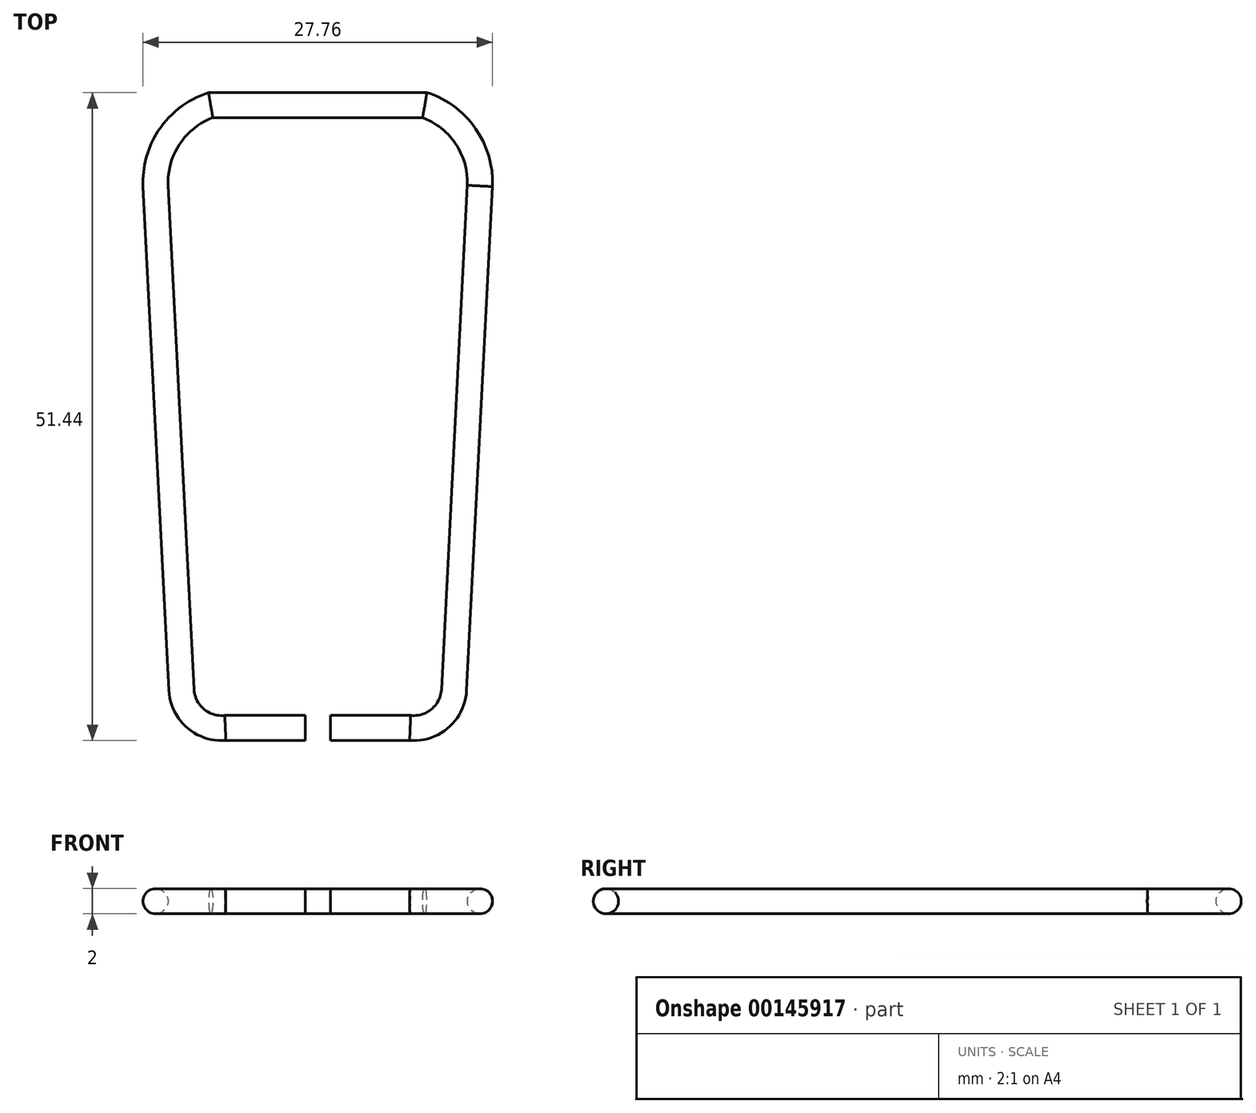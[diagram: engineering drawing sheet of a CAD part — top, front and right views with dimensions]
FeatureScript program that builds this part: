
annotation { "Feature Type Name" : "Feature", "Feature Type Description" : "" }
export const myFeature = defineFeature(function(context is Context, id is Id, definition is map)
    precondition{}
    {
        {
            var Q0;
            Q0=qCreatedBy(makeId("Top.planeOp"),FACE);
            var sketch = newSketch(context, id + "F0", { "sketchPlane" : qUnion([Q0])});
            skArc(sketch, "E0.0", {"start": v(-8.5, 33.52) * mm, "mid": v(-11.75, 31.03) * mm, "end": v(-12.88, 27.1) * mm});
            skLineSegment(sketch, "E0.2", {"start": v(-12.88, 27.1) * mm, "end": v(-10.82, -12.9) * mm});
            skArc(sketch, "E0.4", {"start": v(-10.82, -12.9) * mm, "mid": v(-9.72, -15.15) * mm, "end": v(-7.34, -15.92) * mm});
            skPoint(sketch, "E1.end.orphan", {"position": v(-15, 25.17) * mm});
            skLineSegment(sketch, "E2", {"start": v(-7.34, -15.92) * mm, "end": v(-1, -15.92) * mm});
            skPoint(sketch, "E3", {"position": v(-11.48, 0) * mm});
            skArc(sketch, "E4.MirrorCS", {"start": v(8.5, 33.52) * mm, "mid": v(11.75, 31.03) * mm, "end": v(12.88, 27.1) * mm});
            skLineSegment(sketch, "E5.MirrorCS", {"start": v(12.88, 27.1) * mm, "end": v(10.82, -12.9) * mm});
            skArc(sketch, "E6.MirrorCS", {"start": v(10.82, -12.9) * mm, "mid": v(9.72, -15.15) * mm, "end": v(7.34, -15.92) * mm});
            skLineSegment(sketch, "E7.MirrorCS", {"start": v(7.34, -15.92) * mm, "end": v(1, -15.92) * mm});
            skLineSegment(sketch, "E8", {"start": v(-8.5, 33.52) * mm, "end": v(8.5, 33.52) * mm});
            skSolve(sketch);
        }
        {
            var Q0;
            Q0=qCreatedBy(makeId("Right.planeOp"),FACE);
            cPlane(context, id + "F1", {"entities" : qUnion([Q0]), "cplaneType" : CPlaneType.OFFSET, "offset" : 1 * mm, "width" : 150 * mm, "height" : 150 * mm});
        }
        {
            var Q0;
            Q0=qCreatedBy(id+"F1.planeOp",FACE);
            var sketch = newSketch(context, id + "F2", { "sketchPlane" : qUnion([Q0])});
            skPoint(sketch, "E9.0", {"position": v(-15.92, 0) * mm});
            skCircle(sketch, "E10", {"center": v(-15.92, 0) * mm, "radius": 1 * mm});
            skSolve(sketch);
        }
        {
            var Q0;
            Q0=makeQuery(id+"F2.imprint","IMPRINT",FACE,{"disambiguationData":[TD([[makeQuery(id+"F2.imprint","IMPRINT",EDGE,{"derivedFrom":sQuery(id+"F2.wireOp",EDGE,"E10")}),1.0]])]});
            var Q1;
            Q1=sQuery(id+"F0.wireOp",EDGE,"E7.MirrorCS");
            var Q2;
            Q2=sQuery(id+"F0.wireOp",EDGE,"E6.MirrorCS");
            var Q3;
            Q3=sQuery(id+"F0.wireOp",EDGE,"E5.MirrorCS");
            var Q4;
            Q4=sQuery(id+"F0.wireOp",EDGE,"E4.MirrorCS");
            var Q5;
            Q5=sQuery(id+"F0.wireOp",EDGE,"E8");
            var Q6;
            Q6=sQuery(id+"F0.wireOp",EDGE,"E0.0");
            var Q7;
            Q7=sQuery(id+"F0.wireOp",EDGE,"E0.2");
            var Q8;
            Q8=sQuery(id+"F0.wireOp",EDGE,"E0.4");
            var Q9;
            Q9=sQuery(id+"F0.wireOp",EDGE,"E2");
            sweep(context, id + "F3", {"profiles" : qUnion([Q0]), "path" : qUnion([Q1, Q2, Q3, Q4, Q5, Q6, Q7, Q8, Q9])});
        }
    });
